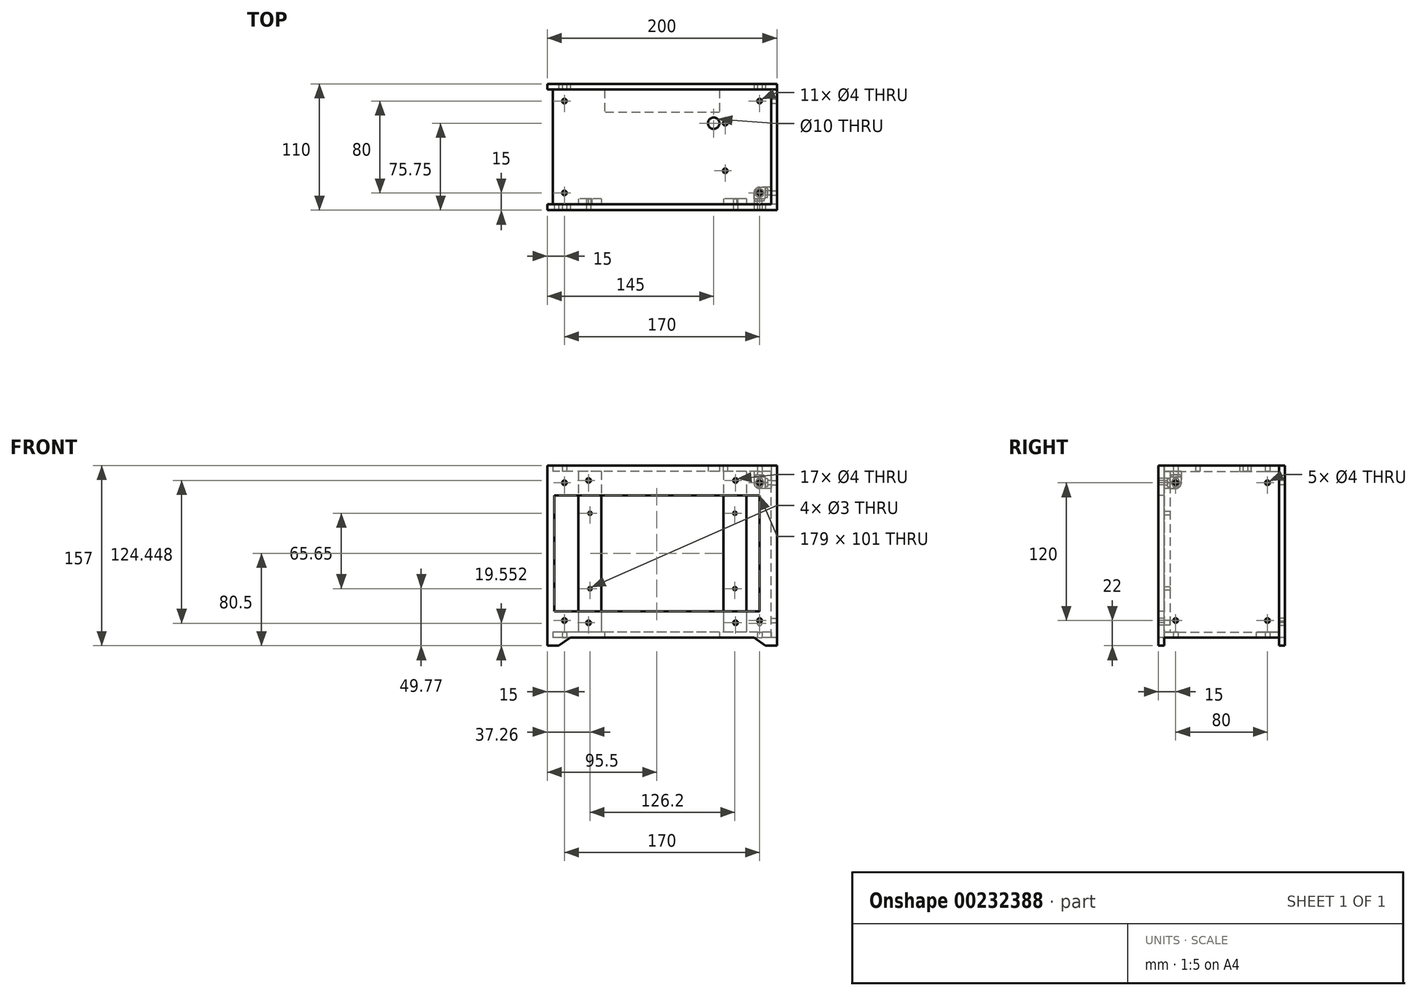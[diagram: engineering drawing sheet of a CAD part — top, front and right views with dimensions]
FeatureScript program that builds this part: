
annotation { "Feature Type Name" : "Feature", "Feature Type Description" : "" }
export const myFeature = defineFeature(function(context is Context, id is Id, definition is map)
    precondition{}
    {
        {
            var Q0;
            Q0=qCreatedBy(makeId("Front.planeOp"),FACE);
            var sketch = newSketch(context, id + "F0", { "sketchPlane" : qUnion([Q0])});
            skLineSegment(sketch, "E0.bottom", {"start": v(100, -75) * mm, "end": v(-100, -75) * mm});
            skLineSegment(sketch, "E0.top", {"start": v(100, 75) * mm, "end": v(-100, 75) * mm});
            skLineSegment(sketch, "E0.left", {"start": v(100, -75) * mm, "end": v(100, 75) * mm});
            skLineSegment(sketch, "E0.right", {"start": v(-100, -75) * mm, "end": v(-100, 75) * mm});
            skPoint(sketch, "E0.middle", {"position": v(0, 0) * mm});
            skSolve(sketch);
        }
        {
            var Q0;
            Q0 = qSketchRegion(id + "F0", true);
            extrude(context, id + "F1", {"entities" : qUnion([Q0]), "depth" : 5 * mm});
        }
        {
            var Q0;
            Q0=makeQuery(id+"F1.opExtrude","CAP_FACE",FACE,{"disambiguationData":[OSD([sQuery(id+"F0.wireOp",EDGE,"E0.bottom"),sQuery(id+"F0.wireOp",EDGE,"E0.top"),sQuery(id+"F0.wireOp",EDGE,"E0.left"),sQuery(id+"F0.wireOp",EDGE,"E0.right")])],"isStart":false});
            var sketch = newSketch(context, id + "F2", { "sketchPlane" : qUnion([Q0])});
            skLineSegment(sketch, "E1.bottom", {"start": v(91, -55) * mm, "end": v(-91, -55) * mm});
            skLineSegment(sketch, "E1.top", {"start": v(91, 55) * mm, "end": v(-91, 55) * mm});
            skLineSegment(sketch, "E1.left", {"start": v(96, -50) * mm, "end": v(96, 50) * mm});
            skLineSegment(sketch, "E1.right", {"start": v(-96, -50) * mm, "end": v(-96, 50) * mm});
            skPoint(sketch, "E1.middle", {"position": v(0, 0) * mm});
            skPoint(sketch, "E2.visualSharp", {"position": v(-96, 55) * mm});
            skArc(sketch, "E2.filletArc", {"start": v(-91, 55) * mm, "mid": v(-94.54, 53.54) * mm, "end": v(-96, 50) * mm});
            skPoint(sketch, "E3.visualSharp", {"position": v(96, 55) * mm});
            skArc(sketch, "E3.filletArc", {"start": v(96, 50) * mm, "mid": v(94.54, 53.54) * mm, "end": v(91, 55) * mm});
            skPoint(sketch, "E4.visualSharp", {"position": v(96, -55) * mm});
            skArc(sketch, "E4.filletArc", {"start": v(91, -55) * mm, "mid": v(94.54, -53.54) * mm, "end": v(96, -50) * mm});
            skPoint(sketch, "E5.visualSharp", {"position": v(-96, -55) * mm});
            skArc(sketch, "E5.filletArc", {"start": v(-96, -50) * mm, "mid": v(-94.54, -53.54) * mm, "end": v(-91, -55) * mm});
            skSolve(sketch);
        }
        {
            var Q0;
            Q0=makeQuery(id+"F2.imprint","IMPRINT",FACE,{"disambiguationData":[TD([[makeQuery(id+"F2.imprint","IMPRINT",EDGE,{"derivedFrom":sQuery(id+"F2.wireOp",EDGE,"E1.bottom")}),1.0]])]});
            var sketch = newSketch(context, id + "F3", { "sketchPlane" : qUnion([Q0])});
            skLineSegment(sketch, "E6.bottom", {"start": v(-94, 49) * mm, "end": v(85, 49) * mm});
            skLineSegment(sketch, "E6.top", {"start": v(-94, -52) * mm, "end": v(85, -52) * mm});
            skLineSegment(sketch, "E6.left", {"start": v(-94, 49) * mm, "end": v(-94, -52) * mm});
            skLineSegment(sketch, "E6.right", {"start": v(85, 49) * mm, "end": v(85, -52) * mm});
            skCircle(sketch, "E7", {"center": v(64, 62) * mm, "radius": 2 * mm});
            skCircle(sketch, "E8", {"center": v(-64, 62) * mm, "radius": 2 * mm});
            skCircle(sketch, "E9", {"center": v(-64, -62) * mm, "radius": 2 * mm});
            skCircle(sketch, "E10", {"center": v(64, -62) * mm, "radius": 2 * mm});
            skCircle(sketch, "E11", {"center": v(85, 60) * mm, "radius": 2 * mm});
            skCircle(sketch, "E12", {"center": v(-85, -60) * mm, "radius": 2 * mm});
            skCircle(sketch, "E13", {"center": v(85, -60) * mm, "radius": 2 * mm});
            skCircle(sketch, "E14", {"center": v(-85, 60) * mm, "radius": 2 * mm});
            skSolve(sketch);
        }
        {
            var Q0;
            Q0 = qSketchRegion(id + "F3", true);
            extrude(context, id + "F4", {"entities" : qUnion([Q0]), "operationType" : NewBodyOperationType.REMOVE, "endBound" : BoundingType.THROUGH_ALL, "oppositeDirection" : true, "depth" : 25 * mm});
        }
        {
            var Q0;
            Q0=makeQuery(id+"F1.opExtrude","CAP_FACE",FACE,{"disambiguationData":[OSD([sQuery(id+"F0.wireOp",EDGE,"E0.bottom"),sQuery(id+"F0.wireOp",EDGE,"E0.top"),sQuery(id+"F0.wireOp",EDGE,"E0.left"),sQuery(id+"F0.wireOp",EDGE,"E0.right")])],"isStart":true});
            var sketch = newSketch(context, id + "F5", { "sketchPlane" : qUnion([Q0])});
            skLineSegment(sketch, "E15.bottom", {"start": v(-73.46, 70) * mm, "end": v(-53.46, 70) * mm});
            skLineSegment(sketch, "E15.top", {"start": v(-73.46, -70) * mm, "end": v(-53.46, -70) * mm});
            skLineSegment(sketch, "E15.left", {"start": v(-73.46, 70) * mm, "end": v(-73.46, -70) * mm});
            skLineSegment(sketch, "E15.right", {"start": v(-53.46, 70) * mm, "end": v(-53.46, -70) * mm});
            skLineSegment(sketch, "E16.bottom", {"start": v(52.74, 70) * mm, "end": v(72.74, 70) * mm});
            skLineSegment(sketch, "E16.top", {"start": v(52.74, -70) * mm, "end": v(72.74, -70) * mm});
            skLineSegment(sketch, "E16.left", {"start": v(52.74, 70) * mm, "end": v(52.74, -70) * mm});
            skLineSegment(sketch, "E16.right", {"start": v(72.74, 70) * mm, "end": v(72.74, -70) * mm});
            skCircle(sketch, "E17", {"center": v(-63.46, 33.42) * mm, "radius": 1.5 * mm});
            skCircle(sketch, "E18", {"center": v(-63.46, -32.23) * mm, "radius": 1.5 * mm});
            skCircle(sketch, "E19", {"center": v(62.74, 33.42) * mm, "radius": 1.5 * mm});
            skCircle(sketch, "E20", {"center": v(62.74, -32.23) * mm, "radius": 1.5 * mm});
            skCircle(sketch, "E21.0", {"center": v(-64, 62) * mm, "radius": 2 * mm});
            skCircle(sketch, "E21.1", {"center": v(-64, -62) * mm, "radius": 2 * mm});
            skCircle(sketch, "E21.2", {"center": v(64, -62) * mm, "radius": 2 * mm});
            skCircle(sketch, "E21.3", {"center": v(64, 62) * mm, "radius": 2 * mm});
            skSolve(sketch);
        }
        {
            var Q0;
            Q0 = qSketchRegion(id + "F5", true);
            extrude(context, id + "F6", {"entities" : qUnion([Q0]), "depth" : 5 * mm});
        }
        {
            var Q0;
            Q0=makeQuery(id+"F1.opExtrude","SWEPT_FACE",FACE,{"disambiguationData":[OSD([sQuery(id+"F0.wireOp",EDGE,"E0.left")])]});
            var sketch = newSketch(context, id + "F7", { "sketchPlane" : qUnion([Q0])});
            skLineSegment(sketch, "E22.0", {"start": v(0, -75) * mm, "end": v(0, 75) * mm});
            skLineSegment(sketch, "E23.bottom", {"start": v(0, 75) * mm, "end": v(100, 75) * mm});
            skLineSegment(sketch, "E23.top", {"start": v(0, -75) * mm, "end": v(100, -75) * mm});
            skLineSegment(sketch, "E23.left", {"start": v(0, 75) * mm, "end": v(0, -75) * mm});
            skLineSegment(sketch, "E23.right", {"start": v(100, 75) * mm, "end": v(100, -75) * mm});
            skCircle(sketch, "E24", {"center": v(10, 60) * mm, "radius": 2 * mm});
            skCircle(sketch, "E25", {"center": v(10, -60) * mm, "radius": 2 * mm});
            skCircle(sketch, "E26", {"center": v(90, -60) * mm, "radius": 2 * mm});
            skCircle(sketch, "E27", {"center": v(90, 60) * mm, "radius": 2 * mm});
            skSolve(sketch);
        }
        {
            var Q0;
            Q0 = qSketchRegion(id + "F7", true);
            extrude(context, id + "F8", {"entities" : qUnion([Q0]), "oppositeDirection" : true, "depth" : 5 * mm});
        }
        {
            var Q0;
            Q0=makeQuery(id+"F6.opExtrude","SWEPT_FACE",FACE,{"disambiguationData":[OSD([sQuery(id+"F5.wireOp",EDGE,"E16.bottom")])]});
            var sketch = newSketch(context, id + "F9", { "sketchPlane" : qUnion([Q0])});
            skLineSegment(sketch, "E28.0", {"start": v(95, 0) * mm, "end": v(95, 100) * mm});
            skLineSegment(sketch, "E29", {"start": v(95, 0) * mm, "end": v(-95, 0) * mm});
            skLineSegment(sketch, "E30", {"start": v(-95, 0) * mm, "end": v(-95, 100) * mm});
            skLineSegment(sketch, "E31", {"start": v(-95, 100) * mm, "end": v(95, 100) * mm});
            skCircle(sketch, "E32", {"center": v(55, 29.25) * mm, "radius": 2 * mm});
            skCircle(sketch, "E33", {"center": v(55, 70.75) * mm, "radius": 2 * mm});
            skLineSegment(sketch, "E34", {"start": v(126.1, 50) * mm, "end": v(-117.06, 50) * mm, "construction": true});
            skPoint(sketch, "E34.startSnap0", {"position": v(95, 50) * mm});
            skPoint(sketch, "E34.endSnap0", {"position": v(95, 50) * mm});
            skLineSegment(sketch, "E35", {"start": v(0, -25.5) * mm, "end": v(0, 175.4) * mm, "construction": true});
            skPoint(sketch, "E35.startSnap0", {"position": v(0, 0) * mm});
            skCircle(sketch, "E36", {"center": v(45, 70.75) * mm, "radius": 5 * mm});
            skCircle(sketch, "E37", {"center": v(85, 10) * mm, "radius": 2 * mm});
            skCircle(sketch, "E38", {"center": v(-85, 90) * mm, "radius": 2 * mm});
            skCircle(sketch, "E39", {"center": v(-85, 10) * mm, "radius": 2 * mm});
            skCircle(sketch, "E40", {"center": v(85, 90) * mm, "radius": 2 * mm});
            skSolve(sketch);
        }
        {
            var Q0;
            Q0 = qSketchRegion(id + "F9", true);
            extrude(context, id + "F10", {"entities" : qUnion([Q0]), "depth" : 5 * mm});
        }
        {
            var Q0;
            Q0=makeQuery(id+"F1.opExtrude","CAP_FACE",FACE,{"disambiguationData":[OSD([sQuery(id+"F0.wireOp",EDGE,"E0.bottom"),sQuery(id+"F0.wireOp",EDGE,"E0.top"),sQuery(id+"F0.wireOp",EDGE,"E0.left"),sQuery(id+"F0.wireOp",EDGE,"E0.right")])],"isStart":true});
            var sketch = newSketch(context, id + "F11", { "sketchPlane" : qUnion([Q0])});
            skLineSegment(sketch, "E41.bottom", {"start": v(-95, 70) * mm, "end": v(-80, 70) * mm});
            skLineSegment(sketch, "E41.top", {"start": v(-95, 55) * mm, "end": v(-80, 55) * mm});
            skLineSegment(sketch, "E41.left", {"start": v(-95, 70) * mm, "end": v(-95, 55) * mm});
            skLineSegment(sketch, "E41.right", {"start": v(-80, 70) * mm, "end": v(-80, 55) * mm});
            skPoint(sketch, "E42.0", {"position": v(-95, 70) * mm});
            skSolve(sketch);
        }
        {
            var Q0;
            Q0 = qSketchRegion(id + "F11", true);
            extrude(context, id + "F12", {"entities" : qUnion([Q0]), "depth" : 15 * mm});
        }
        {
            var Q0;
            Q0=makeQuery(id+"F12.opExtrude","CAP_FACE",FACE,{"disambiguationData":[OSD([sQuery(id+"F11.wireOp",EDGE,"E41.bottom"),sQuery(id+"F11.wireOp",EDGE,"E41.top"),sQuery(id+"F11.wireOp",EDGE,"E41.left"),sQuery(id+"F11.wireOp",EDGE,"E41.right")])],"isStart":false});
            var sketch = newSketch(context, id + "F13", { "sketchPlane" : qUnion([Q0])});
            skLineSegment(sketch, "E43.bottom", {"start": v(-80, 55) * mm, "end": v(-90, 55) * mm});
            skLineSegment(sketch, "E43.top", {"start": v(-80, 65) * mm, "end": v(-90, 65) * mm});
            skLineSegment(sketch, "E43.left", {"start": v(-80, 55) * mm, "end": v(-80, 65) * mm});
            skLineSegment(sketch, "E43.right", {"start": v(-90, 55) * mm, "end": v(-90, 65) * mm});
            skSolve(sketch);
        }
        {
            var Q0;
            Q0 = qSketchRegion(id + "F13", true);
            extrude(context, id + "F14", {"entities" : qUnion([Q0]), "operationType" : NewBodyOperationType.REMOVE, "oppositeDirection" : true, "depth" : 10 * mm});
        }
        {
            var Q0;
            Q0=makeQuery(id+"F14.boolean.opBoolean","COPY",FACE,{"derivedFrom":makeQuery(id+"F14.opExtrude","CAP_FACE",FACE,{"disambiguationData":[OSD([sQuery(id+"F13.wireOp",EDGE,"E43.bottom"),sQuery(id+"F13.wireOp",EDGE,"E43.top"),sQuery(id+"F13.wireOp",EDGE,"E43.left"),sQuery(id+"F13.wireOp",EDGE,"E43.right")])],"isStart":false})});
            var sketch = newSketch(context, id + "F15", { "sketchPlane" : qUnion([Q0])});
            skCircle(sketch, "E44", {"center": v(-85, 60) * mm, "radius": 2 * mm});
            skPoint(sketch, "E44.centerSnap0", {"position": v(-90, 60) * mm});
            skPoint(sketch, "E44.centerSnap1", {"position": v(-85, 65) * mm});
            skSolve(sketch);
        }
        {
            var Q0;
            Q0 = qSketchRegion(id + "F15", true);
            extrude(context, id + "F16", {"entities" : qUnion([Q0]), "operationType" : NewBodyOperationType.REMOVE, "endBound" : BoundingType.THROUGH_ALL, "oppositeDirection" : true, "depth" : 25 * mm});
        }
        {
            var Q0;
            Q0=makeQuery(id+"F12.opExtrude","CAP_EDGE",EDGE,{"disambiguationData":[OSD([sQuery(id+"F11.wireOp",EDGE,"E41.right")])],"isStart":false});
            var Q1;
            Q1=makeQuery(id+"F12.opExtrude","CAP_EDGE",EDGE,{"disambiguationData":[OSD([sQuery(id+"F11.wireOp",EDGE,"E41.top")])],"isStart":false});
            var Q2;
            Q2=makeQuery(id+"F12.opExtrude","SWEPT_EDGE",EDGE,{"disambiguationData":[OSD([sQuery(id+"F11.wireOp",EDGE,"E41.top"),sQuery(id+"F11.wireOp",EDGE,"E41.right")])]});
            fillet(context, id + "F17", {"entities" : qUnion([Q0, Q1, Q2]), "radius" : 5 * mm, "tangentPropagation" : true, "allowEdgeOverflow" : false});
        }
        {
            var Q0;
            Q0=makeQuery(id+"F14.boolean.opBoolean","COPY",FACE,{"derivedFrom":makeQuery(id+"F14.opExtrude","SWEPT_FACE",FACE,{"disambiguationData":[OSD([sQuery(id+"F13.wireOp",EDGE,"E43.top")])]})});
            var sketch = newSketch(context, id + "F18", { "sketchPlane" : qUnion([Q0])});
            skCircle(sketch, "E45", {"center": v(85, -10) * mm, "radius": 2 * mm});
            skPoint(sketch, "E45.centerSnap0", {"position": v(90, -10) * mm});
            skPoint(sketch, "E45.centerSnap1", {"position": v(85, -5) * mm});
            skSolve(sketch);
        }
        {
            var Q0;
            Q0 = qSketchRegion(id + "F18", true);
            extrude(context, id + "F19", {"entities" : qUnion([Q0]), "operationType" : NewBodyOperationType.REMOVE, "endBound" : BoundingType.THROUGH_ALL, "oppositeDirection" : true, "depth" : 25 * mm});
        }
        {
            var Q0;
            Q0=makeQuery(id+"F14.boolean.opBoolean","COPY",FACE,{"derivedFrom":makeQuery(id+"F14.opExtrude","SWEPT_FACE",FACE,{"disambiguationData":[OSD([sQuery(id+"F13.wireOp",EDGE,"E43.right")])]})});
            var sketch = newSketch(context, id + "F20", { "sketchPlane" : qUnion([Q0])});
            skCircle(sketch, "E46", {"center": v(-10, 60) * mm, "radius": 2 * mm});
            skPoint(sketch, "E46.centerSnap0", {"position": v(-5, 60) * mm});
            skPoint(sketch, "E46.centerSnap1", {"position": v(-10, 65) * mm});
            skSolve(sketch);
        }
        {
            var Q0;
            Q0 = qSketchRegion(id + "F20", true);
            extrude(context, id + "F21", {"entities" : qUnion([Q0]), "operationType" : NewBodyOperationType.REMOVE, "endBound" : BoundingType.THROUGH_ALL, "oppositeDirection" : true, "depth" : 25 * mm});
        }
        {
            var Q0;
            Q0=makeQuery(id+"F2.imprint","IMPRINT",FACE,{"disambiguationData":[TD([[makeQuery(id+"F2.imprint","IMPRINT",EDGE,{"derivedFrom":sQuery(id+"F2.wireOp",EDGE,"E1.bottom")}),1.0]])]});
            var sketch = newSketch(context, id + "F22", { "sketchPlane" : qUnion([Q0])});
            skPoint(sketch, "E47.0", {"position": v(-100, -75) * mm});
            skPoint(sketch, "E47.1", {"position": v(100, -75) * mm});
            skLineSegment(sketch, "E48", {"start": v(-100, -75) * mm, "end": v(-100, -82) * mm});
            skLineSegment(sketch, "E49", {"start": v(-100, -82) * mm, "end": v(-90, -82) * mm});
            skLineSegment(sketch, "E50", {"start": v(-90, -82) * mm, "end": v(-80, -75) * mm});
            skLineSegment(sketch, "E51", {"start": v(-80, -75) * mm, "end": v(-100, -75) * mm});
            skLineSegment(sketch, "E52", {"start": v(100, -75) * mm, "end": v(100, -82) * mm});
            skPoint(sketch, "E52.endSnap0", {"position": v(-95, -82) * mm});
            skLineSegment(sketch, "E53", {"start": v(100, -82) * mm, "end": v(90, -82) * mm});
            skLineSegment(sketch, "E54", {"start": v(90, -82) * mm, "end": v(80, -75) * mm});
            skLineSegment(sketch, "E55", {"start": v(80, -75) * mm, "end": v(100, -75) * mm});
            skSolve(sketch);
        }
        {
            var Q0;
            Q0 = qSketchRegion(id + "F22", true);
            extrude(context, id + "F23", {"entities" : qUnion([Q0]), "operationType" : NewBodyOperationType.ADD, "oppositeDirection" : true, "depth" : 5 * mm});
        }
        {
            var Q0;
            Q0=makeQuery(id+"F10.opExtrude","SWEPT_FACE",FACE,{"disambiguationData":[OSD([sQuery(id+"F9.wireOp",EDGE,"E31")])]});
            var sketch = newSketch(context, id + "F24", { "sketchPlane" : qUnion([Q0])});
            skLineSegment(sketch, "E56.bottom", {"start": v(-100, 75) * mm, "end": v(100, 75) * mm});
            skLineSegment(sketch, "E56.top", {"start": v(-100, -75) * mm, "end": v(100, -75) * mm});
            skLineSegment(sketch, "E56.left", {"start": v(-100, 75) * mm, "end": v(-100, -75) * mm});
            skLineSegment(sketch, "E56.right", {"start": v(100, 75) * mm, "end": v(100, -75) * mm});
            skLineSegment(sketch, "E57", {"start": v(-100, -75) * mm, "end": v(-100, -82) * mm});
            skLineSegment(sketch, "E58", {"start": v(-100, -82) * mm, "end": v(-90, -82) * mm});
            skLineSegment(sketch, "E59", {"start": v(-90, -82) * mm, "end": v(-80, -75) * mm});
            skLineSegment(sketch, "E60", {"start": v(100, -75) * mm, "end": v(100, -82) * mm});
            skLineSegment(sketch, "E61", {"start": v(100, -82) * mm, "end": v(90, -82) * mm});
            skLineSegment(sketch, "E62", {"start": v(90, -82) * mm, "end": v(80, -75) * mm});
            skCircle(sketch, "E63", {"center": v(-85, 60) * mm, "radius": 2 * mm});
            skCircle(sketch, "E64", {"center": v(85, 60) * mm, "radius": 2 * mm});
            skCircle(sketch, "E65", {"center": v(85, -60) * mm, "radius": 2 * mm});
            skCircle(sketch, "E66", {"center": v(-85, -62.45) * mm, "radius": 2 * mm});
            skSolve(sketch);
        }
        {
            var Q0;
            Q0 = qSketchRegion(id + "F24", true);
            extrude(context, id + "F25", {"entities" : qUnion([Q0]), "depth" : 5 * mm});
        }
        {
            var Q0;
            Q0=makeQuery(id+"F8.opExtrude","SWEPT_FACE",FACE,{"disambiguationData":[OSD([sQuery(id+"F7.wireOp",EDGE,"E23.top")])]});
            var sketch = newSketch(context, id + "F26", { "sketchPlane" : qUnion([Q0])});
            skLineSegment(sketch, "E67.bottom", {"start": v(95, -100) * mm, "end": v(-95, -100) * mm});
            skLineSegment(sketch, "E67.top", {"start": v(95, 0) * mm, "end": v(-95, 0) * mm});
            skLineSegment(sketch, "E67.left", {"start": v(95, -100) * mm, "end": v(95, 0) * mm});
            skLineSegment(sketch, "E67.right", {"start": v(-95, -100) * mm, "end": v(-95, 0) * mm});
            skCircle(sketch, "E68", {"center": v(85, -90) * mm, "radius": 2 * mm});
            skCircle(sketch, "E69", {"center": v(-85, -90) * mm, "radius": 2 * mm});
            skCircle(sketch, "E70", {"center": v(-85, -10) * mm, "radius": 2 * mm});
            skCircle(sketch, "E71", {"center": v(85, -10) * mm, "radius": 2 * mm});
            skLineSegment(sketch, "E72.bottom", {"start": v(50, -100) * mm, "end": v(-50, -100) * mm});
            skLineSegment(sketch, "E72.top", {"start": v(50, -80) * mm, "end": v(-50, -80) * mm});
            skLineSegment(sketch, "E72.left", {"start": v(50, -100) * mm, "end": v(50, -80) * mm});
            skLineSegment(sketch, "E72.right", {"start": v(-50, -100) * mm, "end": v(-50, -80) * mm});
            skLineSegment(sketch, "E73", {"start": v(0, -119.08) * mm, "end": v(0, 23.06) * mm, "construction": true});
            skPoint(sketch, "E73.startSnap0", {"position": v(0, -100) * mm});
            skSolve(sketch);
        }
        {
            var Q0;
            Q0=makeQuery(id+"F26.imprint","IMPRINT",FACE,{"disambiguationData":[TD([[makeQuery(id+"F26.imprint","IMPRINT",EDGE,{"derivedFrom":sQuery(id+"F26.wireOp",EDGE,"E67.top")}),1.0]])]});
            extrude(context, id + "F27", {"entities" : qUnion([Q0]), "oppositeDirection" : true, "depth" : 5 * mm});
        }
        {
            var Q0;
            Q0=makeQuery(id+"F14.boolean.opBoolean","COPY",FACE,{"derivedFrom":makeQuery(id+"F14.opExtrude","SWEPT_FACE",FACE,{"disambiguationData":[OSD([sQuery(id+"F13.wireOp",EDGE,"E43.right")])]})});
            var sketch = newSketch(context, id + "F28", { "sketchPlane" : qUnion([Q0])});
            skCircle(sketch, "E74.cCircle", {"center": v(-10, 60) * mm, "radius": 3.5 * mm, "construction": true});
            skLineSegment(sketch, "E74.0", {"start": v(-7.98, 56.5) * mm, "end": v(-12.02, 56.5) * mm});
            skLineSegment(sketch, "E74.1", {"start": v(-12.02, 56.5) * mm, "end": v(-14.04, 60) * mm});
            skLineSegment(sketch, "E74.2", {"start": v(-14.04, 60) * mm, "end": v(-12.02, 63.5) * mm});
            skLineSegment(sketch, "E74.3", {"start": v(-12.02, 63.5) * mm, "end": v(-7.98, 63.5) * mm});
            skLineSegment(sketch, "E74.4", {"start": v(-7.98, 63.5) * mm, "end": v(-5.96, 60) * mm});
            skLineSegment(sketch, "E74.5", {"start": v(-5.96, 60) * mm, "end": v(-7.98, 56.5) * mm});
            skPoint(sketch, "E74.0.midPoint", {"position": v(-10, 56.5) * mm});
            skSolve(sketch);
        }
        {
            var Q0;
            Q0=makeQuery(id+"F28.imprint","IMPRINT",FACE,{"disambiguationData":[TD([[makeQuery(id+"F28.imprint","IMPRINT",EDGE,{"derivedFrom":sQuery(id+"F28.wireOp",EDGE,"E74.0")}),-1.0]])]});
            extrude(context, id + "F29", {"entities" : qUnion([Q0]), "operationType" : NewBodyOperationType.REMOVE, "oppositeDirection" : true, "depth" : 2 * mm});
        }
        {
            var Q0;
            Q0=makeQuery(id+"F14.boolean.opBoolean","COPY",FACE,{"derivedFrom":makeQuery(id+"F14.opExtrude","SWEPT_FACE",FACE,{"disambiguationData":[OSD([sQuery(id+"F13.wireOp",EDGE,"E43.top")])]})});
            var sketch = newSketch(context, id + "F30", { "sketchPlane" : qUnion([Q0])});
            skCircle(sketch, "E75.cCircle", {"center": v(85, -10) * mm, "radius": 3.5 * mm, "construction": true});
            skLineSegment(sketch, "E75.0", {"start": v(88.5, -7.98) * mm, "end": v(88.5, -12.02) * mm});
            skLineSegment(sketch, "E75.1", {"start": v(88.5, -12.02) * mm, "end": v(85, -14.04) * mm});
            skLineSegment(sketch, "E75.2", {"start": v(85, -14.04) * mm, "end": v(81.5, -12.02) * mm});
            skLineSegment(sketch, "E75.3", {"start": v(81.5, -12.02) * mm, "end": v(81.5, -7.98) * mm});
            skLineSegment(sketch, "E75.4", {"start": v(81.5, -7.98) * mm, "end": v(85, -5.96) * mm});
            skLineSegment(sketch, "E75.5", {"start": v(85, -5.96) * mm, "end": v(88.5, -7.98) * mm});
            skPoint(sketch, "E75.0.midPoint", {"position": v(88.5, -10) * mm});
            skSolve(sketch);
        }
        {
            var Q0;
            Q0 = qSketchRegion(id + "F30", true);
            extrude(context, id + "F31", {"entities" : qUnion([Q0]), "operationType" : NewBodyOperationType.REMOVE, "oppositeDirection" : true, "depth" : 2 * mm});
        }
        {
            var Q0;
            Q0=makeQuery(id+"F14.boolean.opBoolean","COPY",FACE,{"derivedFrom":makeQuery(id+"F14.opExtrude","CAP_FACE",FACE,{"disambiguationData":[OSD([sQuery(id+"F13.wireOp",EDGE,"E43.bottom"),sQuery(id+"F13.wireOp",EDGE,"E43.top"),sQuery(id+"F13.wireOp",EDGE,"E43.left"),sQuery(id+"F13.wireOp",EDGE,"E43.right")])],"isStart":false})});
            var sketch = newSketch(context, id + "F32", { "sketchPlane" : qUnion([Q0])});
            skCircle(sketch, "E76.cCircle", {"center": v(-85, 60) * mm, "radius": 3.5 * mm, "construction": true});
            skLineSegment(sketch, "E76.0", {"start": v(-87.02, 63.5) * mm, "end": v(-82.98, 63.5) * mm});
            skLineSegment(sketch, "E76.1", {"start": v(-82.98, 63.5) * mm, "end": v(-80.96, 60) * mm});
            skLineSegment(sketch, "E76.2", {"start": v(-80.96, 60) * mm, "end": v(-82.98, 56.5) * mm});
            skLineSegment(sketch, "E76.3", {"start": v(-82.98, 56.5) * mm, "end": v(-87.02, 56.5) * mm});
            skLineSegment(sketch, "E76.4", {"start": v(-87.02, 56.5) * mm, "end": v(-89.04, 60) * mm});
            skLineSegment(sketch, "E76.5", {"start": v(-89.04, 60) * mm, "end": v(-87.02, 63.5) * mm});
            skPoint(sketch, "E76.0.midPoint", {"position": v(-85, 63.5) * mm});
            skSolve(sketch);
        }
        {
            var Q0;
            Q0 = qSketchRegion(id + "F32", true);
            extrude(context, id + "F33", {"entities" : qUnion([Q0]), "operationType" : NewBodyOperationType.REMOVE, "oppositeDirection" : true, "depth" : 2 * mm});
        }
    });
